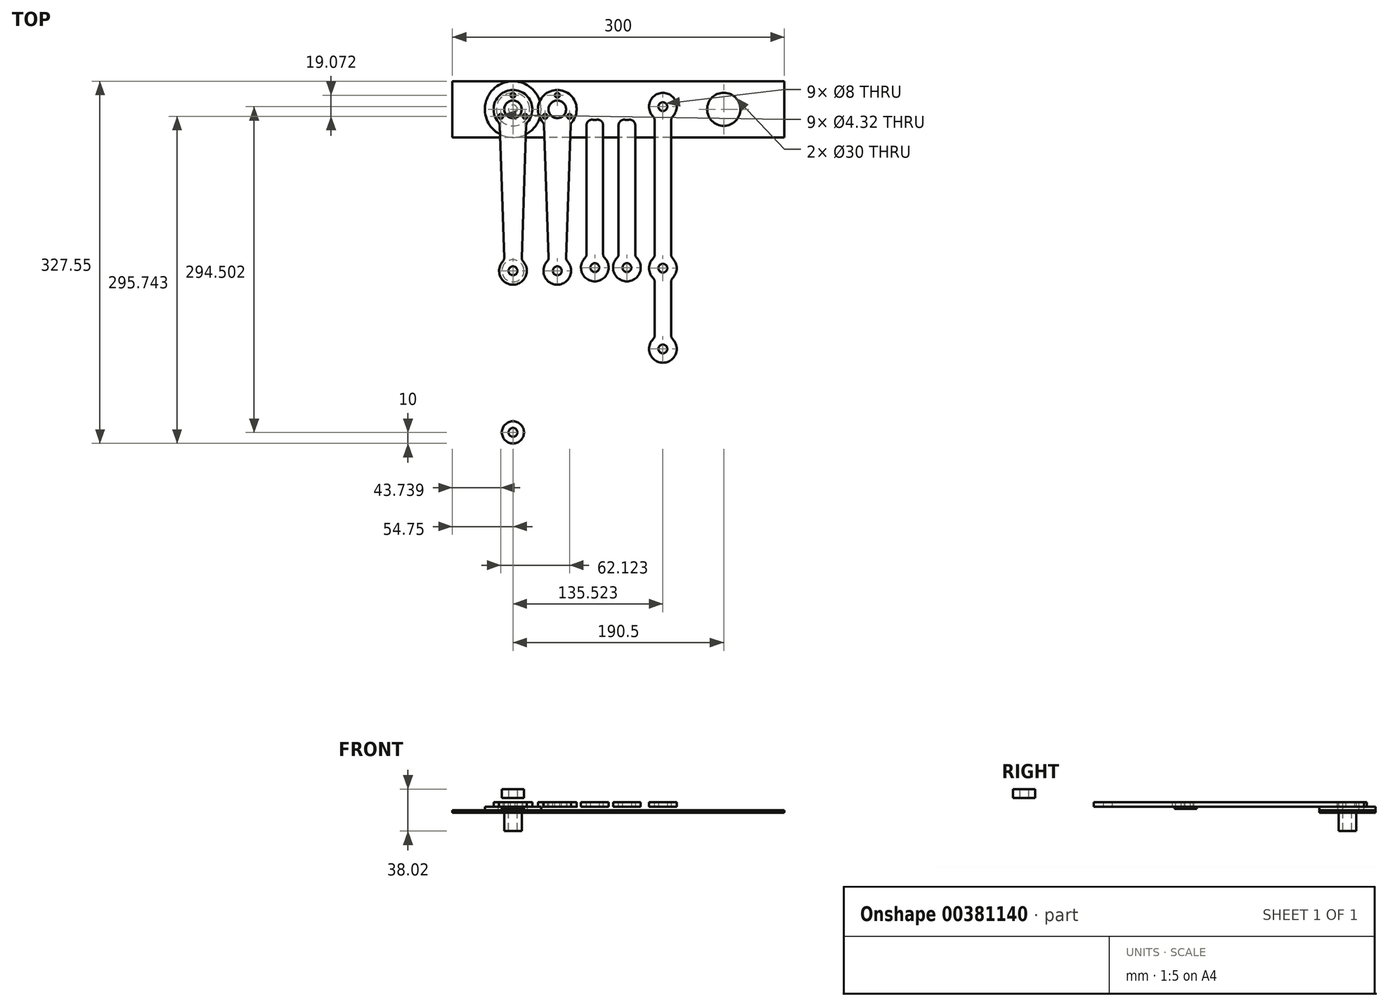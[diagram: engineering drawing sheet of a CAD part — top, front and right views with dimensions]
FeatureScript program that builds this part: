
annotation { "Feature Type Name" : "Feature", "Feature Type Description" : "" }
export const myFeature = defineFeature(function(context is Context, id is Id, definition is map)
    precondition{}
    {
        {
            var Q0;
            Q0=qCreatedBy(makeId("Top.planeOp"),FACE);
            var sketch = newSketch(context, id + "F0", { "sketchPlane" : qUnion([Q0])});
            skCircle(sketch, "E0", {"center": v(0, 0) * mm, "radius": 25.4 * mm});
            skCircle(sketch, "E1", {"center": v(0, 0) * mm, "radius": 7.93 * mm});
            skCircle(sketch, "E2", {"center": v(0, 0) * mm, "radius": 4 * mm});
            skSolve(sketch);
        }
        {
            var Q0;
            Q0=makeQuery(id+"F0.imprint","IMPRINT",FACE,{"disambiguationData":[TD([[makeQuery(id+"F0.imprint","IMPRINT",EDGE,{"derivedFrom":sQuery(id+"F0.wireOp",EDGE,"E0")}),1.0]])]});
            var Q1;
            Q1=makeQuery(id+"F0.imprint","IMPRINT",FACE,{"disambiguationData":[TD([[makeQuery(id+"F0.imprint","IMPRINT",EDGE,{"derivedFrom":sQuery(id+"F0.wireOp",EDGE,"E1")}),1.0]])]});
            var Q2;
            Q2=makeQuery(id+"F0.imprint","IMPRINT",FACE,{"disambiguationData":[TD([[makeQuery(id+"F0.imprint","IMPRINT",EDGE,{"derivedFrom":sQuery(id+"F0.wireOp",EDGE,"E2")}),1.0]])]});
            var Q3;
            Q3=sQuery(id+"F0.wireOp",EDGE,"E0");
            var Q4;
            Q4=sQuery(id+"F0.wireOp",EDGE,"E1");
            var Q5;
            Q5=sQuery(id+"F0.wireOp",EDGE,"E2");
            extrude(context, id + "F1", {"entities" : qUnion([Q0, Q1, Q2]), "surfaceEntities" : qUnion([Q3, Q4, Q5]), "depth" : 3.17 * mm});
        }
        {
            var Q0;
            Q0=makeQuery(id+"F0.imprint","IMPRINT",FACE,{"disambiguationData":[TD([[makeQuery(id+"F0.imprint","IMPRINT",EDGE,{"derivedFrom":sQuery(id+"F0.wireOp",EDGE,"E1")}),1.0]])]});
            extrude(context, id + "F2", {"entities" : qUnion([Q0]), "operationType" : NewBodyOperationType.ADD, "oppositeDirection" : true, "depth" : 18.85 * mm});
        }
        {
            var Q0;
            Q0=makeQuery(id+"F1.opExtrude","CAP_FACE",FACE,{"disambiguationData":[OSD([sQuery(id+"F0.wireOp",EDGE,"E0")])],"isStart":false});
            var sketch = newSketch(context, id + "F3", { "sketchPlane" : qUnion([Q0])});
            skLineSegment(sketch, "E3", {"start": v(-17.51, 0) * mm, "end": v(-12.5, -146.05) * mm});
            skLineSegment(sketch, "E4", {"start": v(17.51, 0) * mm, "end": v(12.5, -146.05) * mm});
            skCircle(sketch, "E5", {"center": v(0, 0) * mm, "radius": 17.5 * mm});
            skCircle(sketch, "E6", {"center": v(0, -146.05) * mm, "radius": 12.5 * mm});
            skLineSegment(sketch, "E7", {"start": v(-12.07, -12.67) * mm, "end": v(-7.83, -136.3) * mm});
            skLineSegment(sketch, "E8", {"start": v(12.07, -12.67) * mm, "end": v(7.84, -136.31) * mm});
            skCircle(sketch, "E9.0", {"center": v(0, 0) * mm, "radius": 7.93 * mm});
            skSolve(sketch);
        }
        {
            var Q0;
            {var subQ0=sQuery(id+"F3.wireOp",EDGE,"E5");var subQ1=makeQuery(id+"F3.imprint","INTERSECT",VERTEX,{"derivedFrom":[sQuery(id+"F3.wireOp",EDGE,"E3"),subQ0]});Q0=makeQuery(id+"F3.imprint","IMPRINT",FACE,{"disambiguationData":[TD([[makeQuery(id+"F3.imprint","IMPRINT",EDGE,{"disambiguationData":[TD([[subQ1,1.0]])],"derivedFrom":subQ0}),1.0]])]});}
            var Q1;
            {var subQ0=sQuery(id+"F3.wireOp",EDGE,"E7");var subQ1=sQuery(id+"F3.wireOp",EDGE,"E5");var subQ2=makeQuery(id+"F3.imprint","INTERSECT",VERTEX,{"derivedFrom":[subQ1,subQ0]});Q1=makeQuery(id+"F3.imprint","IMPRINT",FACE,{"disambiguationData":[TD([[makeQuery(id+"F3.imprint","IMPRINT",EDGE,{"disambiguationData":[TD([[subQ2,-1.0]])],"derivedFrom":subQ1}),-1.0]])]});}
            var Q2;
            {var subQ0=sQuery(id+"F3.wireOp",EDGE,"E6");var subQ1=makeQuery(id+"F3.imprint","INTERSECT",VERTEX,{"derivedFrom":[sQuery(id+"F3.wireOp",EDGE,"E4"),subQ0]});Q2=makeQuery(id+"F3.imprint","IMPRINT",FACE,{"disambiguationData":[TD([[makeQuery(id+"F3.imprint","IMPRINT",EDGE,{"disambiguationData":[TD([[subQ1,-1.0]])],"derivedFrom":subQ0}),1.0]])]});}
            var Q3;
            {var subQ0=sQuery(id+"F3.wireOp",EDGE,"E7");var subQ1=sQuery(id+"F3.wireOp",EDGE,"E6");var subQ2=makeQuery(id+"F3.imprint","INTERSECT",VERTEX,{"derivedFrom":[subQ1,subQ0]});Q3=makeQuery(id+"F3.imprint","IMPRINT",FACE,{"disambiguationData":[TD([[makeQuery(id+"F3.imprint","IMPRINT",EDGE,{"disambiguationData":[TD([[subQ2,1.0]])],"derivedFrom":subQ1}),-1.0]])]});}
            extrude(context, id + "F4", {"entities" : qUnion([Q0, Q1, Q2, Q3]), "depth" : 4 * mm});
        }
        {
            var Q0;
            Q0=makeQuery(id+"F4.opExtrude","SWEPT_EDGE",EDGE,{"disambiguationData":[OSD([sQuery(id+"F3.wireOp",EDGE,"E5"),sQuery(id+"F3.wireOp",EDGE,"E7")])]});
            var Q1;
            Q1=makeQuery(id+"F4.opExtrude","SWEPT_EDGE",EDGE,{"disambiguationData":[OSD([sQuery(id+"F3.wireOp",EDGE,"E5"),sQuery(id+"F3.wireOp",EDGE,"E8")])]});
            var Q2;
            Q2=makeQuery(id+"F4.opExtrude","SWEPT_EDGE",EDGE,{"disambiguationData":[OSD([sQuery(id+"F3.wireOp",EDGE,"E6"),sQuery(id+"F3.wireOp",EDGE,"E7")])]});
            var Q3;
            Q3=makeQuery(id+"F4.opExtrude","SWEPT_EDGE",EDGE,{"disambiguationData":[OSD([sQuery(id+"F3.wireOp",EDGE,"E6"),sQuery(id+"F3.wireOp",EDGE,"E8")])]});
            fillet(context, id + "F5", {"entities" : qUnion([Q0, Q1, Q2, Q3]), "radius" : 5 * mm, "tangentPropagation" : true, "allowEdgeOverflow" : false});
        }
        {
            var Q0;
            Q0=makeQuery(id+"F4.opExtrude","CAP_FACE",FACE,{"disambiguationData":[OSD([sQuery(id+"F3.wireOp",EDGE,"E5"),sQuery(id+"F3.wireOp",EDGE,"E6"),sQuery(id+"F3.wireOp",EDGE,"E7"),sQuery(id+"F3.wireOp",EDGE,"E8")])],"isStart":false});
            var sketch = newSketch(context, id + "F6", { "sketchPlane" : qUnion([Q0])});
            skPoint(sketch, "E10.center", {"position": v(0, 0) * mm});
            skCircle(sketch, "E11", {"center": v(0, -146.05) * mm, "radius": 4 * mm});
            skPoint(sketch, "E12", {"position": v(0, 12.71) * mm});
            skPoint(sketch, "E13.1.0", {"position": v(-11.01, -6.36) * mm});
            skPoint(sketch, "E13.2.0", {"position": v(11.01, -6.36) * mm});
            skSolve(sketch);
        }
        {
            var Q0;
            Q0=makeQuery(id+"F6.imprint","IMPRINT",FACE,{"disambiguationData":[TD([[makeQuery(id+"F6.imprint","IMPRINT",EDGE,{"derivedFrom":sQuery(id+"F6.wireOp",EDGE,"PpWmp2N7-R2N7-yGAy-fFJR-1MrLJnRTjxl5")}),1.0]])]});
            var Q1;
            Q1=makeQuery(id+"F6.imprint","IMPRINT",FACE,{"disambiguationData":[TD([[makeQuery(id+"F6.imprint","IMPRINT",EDGE,{"derivedFrom":sQuery(id+"F6.wireOp",EDGE,"E10.2.0")}),1.0]])]});
            var Q2;
            Q2=makeQuery(id+"F6.imprint","IMPRINT",FACE,{"disambiguationData":[TD([[makeQuery(id+"F6.imprint","IMPRINT",EDGE,{"derivedFrom":sQuery(id+"F6.wireOp",EDGE,"E10.1.0")}),1.0]])]});
            var Q3;
            Q3=makeQuery(id+"F6.imprint","IMPRINT",FACE,{"disambiguationData":[TD([[makeQuery(id+"F6.imprint","IMPRINT",EDGE,{"derivedFrom":sQuery(id+"F6.wireOp",EDGE,"E11")}),1.0]])]});
            extrude(context, id + "F7", {"entities" : qUnion([Q0, Q1, Q2, Q3]), "operationType" : NewBodyOperationType.REMOVE, "endBound" : BoundingType.THROUGH_ALL, "oppositeDirection" : true, "depth" : 25 * mm});
        }
        {
            var Q0;
            Q0=makeQuery(id+"F4.opExtrude","CAP_FACE",FACE,{"disambiguationData":[OSD([sQuery(id+"F3.wireOp",EDGE,"E5"),sQuery(id+"F3.wireOp",EDGE,"E6"),sQuery(id+"F3.wireOp",EDGE,"E7"),sQuery(id+"F3.wireOp",EDGE,"E8")])],"isStart":true});
            var sketch = newSketch(context, id + "F8", { "sketchPlane" : qUnion([Q0])});
            skCircle(sketch, "E14", {"center": v(0, 146.05) * mm, "radius": 10 * mm});
            skCircle(sketch, "E15.0", {"center": v(0, 146.05) * mm, "radius": 4 * mm});
            skSolve(sketch);
        }
        {
            var Q0;
            Q0=makeQuery(id+"F8.imprint","IMPRINT",FACE,{"disambiguationData":[TD([[makeQuery(id+"F8.imprint","IMPRINT",EDGE,{"derivedFrom":sQuery(id+"F8.wireOp",EDGE,"E14")}),1.0]])]});
            extrude(context, id + "F9", {"entities" : qUnion([Q0]), "depth" : 2 * mm});
        }
        {
            var Q0;
            {var subQ0=sQuery(id+"F0.wireOp",EDGE,"E0");Q0=makeQuery(id+"F2.boolean.opBoolean","SPLIT",FACE,{"disambiguationData":[TD([makeQuery(id+"F1.opExtrude","SWEPT_FACE",FACE,{"disambiguationData":[OSD([subQ0])]})])],"derivedFrom":makeQuery(id+"F1.opExtrude","CAP_FACE",FACE,{"disambiguationData":[OSD([subQ0])],"isStart":true})});}
            var sketch = newSketch(context, id + "F10", { "sketchPlane" : qUnion([Q0])});
            skCircle(sketch, "E16", {"center": v(0, 0) * mm, "radius": 15 * mm});
            skCircle(sketch, "E17", {"center": v(190.5, 0) * mm, "radius": 15 * mm});
            skLineSegment(sketch, "E18.bottom", {"start": v(245.25, -25.45) * mm, "end": v(-54.75, -25.45) * mm});
            skLineSegment(sketch, "E18.top", {"start": v(245.25, 25.45) * mm, "end": v(-54.75, 25.45) * mm});
            skLineSegment(sketch, "E18.left", {"start": v(245.25, -25.45) * mm, "end": v(245.25, 25.45) * mm});
            skLineSegment(sketch, "E18.right", {"start": v(-54.75, -25.45) * mm, "end": v(-54.75, 25.45) * mm});
            skLineSegment(sketch, "E19", {"start": v(245.25, 0) * mm, "end": v(-54.75, 0) * mm, "construction": true});
            skLineSegment(sketch, "E20", {"start": v(95.25, -25.45) * mm, "end": v(95.25, 25.45) * mm, "construction": true});
            skSolve(sketch);
        }
        {
            var Q0;
            Q0=makeQuery(id+"F10.imprint","IMPRINT",FACE,{"disambiguationData":[TD([[makeQuery(id+"F10.imprint","IMPRINT",EDGE,{"derivedFrom":sQuery(id+"F10.wireOp",EDGE,"E17")}),-1.0]])]});
            var Q1;
            Q1=makeQuery(id+"F10.imprint","IMPRINT",FACE,{"disambiguationData":[TD([[makeQuery(id+"F10.imprint","IMPRINT",EDGE,{"derivedFrom":sQuery(id+"F10.wireOp",EDGE,"E16")}),-1.0]])]});
            extrude(context, id + "F11", {"entities" : qUnion([Q0, Q1]), "depth" : 2.3 * mm});
        }
        {
            var Q0;
            Q0=makeQuery(id+"F4.opExtrude","CAP_FACE",FACE,{"disambiguationData":[OSD([sQuery(id+"F3.wireOp",EDGE,"E5"),sQuery(id+"F3.wireOp",EDGE,"E6"),sQuery(id+"F3.wireOp",EDGE,"E7"),sQuery(id+"F3.wireOp",EDGE,"E8")])],"isStart":false});
            var sketch = newSketch(context, id + "F12", { "sketchPlane" : qUnion([Q0])});
            skLineSegment(sketch, "E21", {"start": v(-12.5, -146.05) * mm, "end": v(-12.5, -292.1) * mm});
            skLineSegment(sketch, "E22", {"start": v(12.5, -146.05) * mm, "end": v(12.5, -292.1) * mm});
            skCircle(sketch, "E23", {"center": v(0, -146.05) * mm, "radius": 12.5 * mm});
            skCircle(sketch, "E24", {"center": v(0, -292.1) * mm, "radius": 12.5 * mm});
            skLineSegment(sketch, "E25", {"start": v(-7.5, -156.05) * mm, "end": v(-7.5, -282.1) * mm});
            skLineSegment(sketch, "E26", {"start": v(7.5, -156.05) * mm, "end": v(7.5, -282.1) * mm});
            skCircle(sketch, "E27", {"center": v(0, -292.1) * mm, "radius": 4 * mm});
            skSolve(sketch);
        }
        {
            var Q0;
            Q0=makeQuery(id+"F12.imprint","IMPRINT",FACE,{"disambiguationData":[TD([[makeQuery(id+"F12.imprint","IMPRINT",EDGE,{"derivedFrom":makeQuery(id+"F7.boolean.opBoolean","COPY",EDGE,{"derivedFrom":makeQuery(id+"F7.opExtrude","CAP_EDGE",EDGE,{"disambiguationData":[OSD([sQuery(id+"F6.wireOp",EDGE,"E11")])],"isStart":true})})}),-1.0]])]});
            var Q1;
            {var subQ0=sQuery(id+"F12.wireOp",EDGE,"E25");Q1=makeQuery(id+"F12.imprint","IMPRINT",FACE,{"disambiguationData":[TD([[makeQuery(id+"F12.imprint","IMPRINT",EDGE,{"derivedFrom":subQ0}),1.0]])]});}
            var Q2;
            Q2=makeQuery(id+"F12.imprint","IMPRINT",FACE,{"disambiguationData":[TD([[makeQuery(id+"F12.imprint","IMPRINT",EDGE,{"derivedFrom":sQuery(id+"F12.wireOp",EDGE,"E27")}),-1.0]])]});
            extrude(context, id + "F13", {"entities" : qUnion([Q0, Q1, Q2]), "depth" : 4 * mm});
        }
        {
            var Q0;
            Q0=makeQuery(id+"F13.opExtrude","SWEPT_EDGE",EDGE,{"disambiguationData":[OSD([sQuery(id+"F12.wireOp",EDGE,"E23"),sQuery(id+"F12.wireOp",EDGE,"E25")])]});
            var Q1;
            Q1=makeQuery(id+"F13.opExtrude","SWEPT_EDGE",EDGE,{"disambiguationData":[OSD([sQuery(id+"F12.wireOp",EDGE,"E24"),sQuery(id+"F12.wireOp",EDGE,"E25")])]});
            var Q2;
            Q2=makeQuery(id+"F13.opExtrude","SWEPT_EDGE",EDGE,{"disambiguationData":[OSD([sQuery(id+"F12.wireOp",EDGE,"E23"),sQuery(id+"F12.wireOp",EDGE,"E26")])]});
            var Q3;
            Q3=makeQuery(id+"F13.opExtrude","SWEPT_EDGE",EDGE,{"disambiguationData":[OSD([sQuery(id+"F12.wireOp",EDGE,"E24"),sQuery(id+"F12.wireOp",EDGE,"E26")])]});
            fillet(context, id + "F14", {"entities" : qUnion([Q0, Q1, Q2, Q3]), "radius" : 5 * mm, "tangentPropagation" : true, "allowEdgeOverflow" : false});
        }
        {
            var Q0;
            Q0=makeQuery(id+"F13.opExtrude","CAP_FACE",FACE,{"disambiguationData":[OSD([sQuery(id+"F6.wireOp",EDGE,"E11"),sQuery(id+"F12.wireOp",EDGE,"E23"),sQuery(id+"F12.wireOp",EDGE,"E24"),sQuery(id+"F12.wireOp",EDGE,"E25"),sQuery(id+"F12.wireOp",EDGE,"E26"),sQuery(id+"F12.wireOp",EDGE,"E27")])],"isStart":false});
            var sketch = newSketch(context, id + "F15", { "sketchPlane" : qUnion([Q0])});
            skCircle(sketch, "E28", {"center": v(0, -292.1) * mm, "radius": 10 * mm});
            skSolve(sketch);
        }
        {
            var Q0;
            Q0=makeQuery(id+"F15.imprint","IMPRINT",FACE,{"disambiguationData":[TD([[makeQuery(id+"F15.imprint","IMPRINT",EDGE,{"derivedFrom":sQuery(id+"F15.wireOp",EDGE,"E28")}),1.0]])]});
            extrude(context, id + "F16", {"entities" : qUnion([Q0]), "depth" : 8 * mm});
        }
        {
            var Q0;
            Q0=sQuery(id+"F6.wireOp",VERTEX,"E12");
            var Q1;
            Q1=sQuery(id+"F6.wireOp",VERTEX,"E13.2.0");
            var Q2;
            Q2=sQuery(id+"F6.wireOp",VERTEX,"E13.1.0");
            var Q3;
            Q3=makeQuery(id+"F1.opExtrude","SWEPT_BODY",BODY,{"disambiguationData":[OSD([sQuery(id+"F0.wireOp",EDGE,"E0")])]});
            var Q4;
            Q4=makeQuery(id+"F4.opExtrude","SWEPT_BODY",BODY,{"disambiguationData":[OSD([sQuery(id+"F3.wireOp",EDGE,"E5"),sQuery(id+"F3.wireOp",EDGE,"E6"),sQuery(id+"F3.wireOp",EDGE,"E7"),sQuery(id+"F3.wireOp",EDGE,"E8"),sQuery(id+"F3.wireOp",EDGE,"E9.0")])]});
            hole(context, id + "F17", {"style" : HoleStyle.SIMPLE, "endStyle" : HoleEndStyle.THROUGH, "standardTappedOrClearance" : lookupTablePath({ "standard" : "ANSI", "fit" : "Close", "size" : "#8", "type" : "Clearance" }), "standardBlindInLast" : lookupTablePath({ "fit" : "Close", "standard" : "ANSI", "size" : "#8", "type" : "Clearance" }), "holeDiameter" : 4.32 * mm, "isTappedThrough" : true, "tappedDepth" : 6.2 * mm, "tapClearance" : 3, "locations" : qUnion([Q0, Q1, Q2]), "scope" : qUnion([Q3, Q4])});
        }
        {
            var Q0;
            Q0=makeQuery(id+"F13.opExtrude","CAP_FACE",FACE,{"disambiguationData":[OSD([sQuery(id+"F6.wireOp",EDGE,"E11"),sQuery(id+"F12.wireOp",EDGE,"E23"),sQuery(id+"F12.wireOp",EDGE,"E24"),sQuery(id+"F12.wireOp",EDGE,"E25"),sQuery(id+"F12.wireOp",EDGE,"E26"),sQuery(id+"F12.wireOp",EDGE,"E27")])],"isStart":false});
            var sketch = newSketch(context, id + "F18", { "sketchPlane" : qUnion([Q0])});
            skLineSegment(sketch, "E29", {"start": v(44.92, -100.2) * mm, "end": v(44.92, -246.25) * mm});
            skLineSegment(sketch, "E30", {"start": v(69.92, -100.2) * mm, "end": v(69.92, -246.25) * mm});
            skCircle(sketch, "E31", {"center": v(57.42, -100.2) * mm, "radius": 12.5 * mm});
            skCircle(sketch, "E32", {"center": v(57.42, -246.25) * mm, "radius": 12.5 * mm});
            skLineSegment(sketch, "E33", {"start": v(49.92, -110.2) * mm, "end": v(49.92, -236.25) * mm});
            skLineSegment(sketch, "E34", {"start": v(64.92, -110.2) * mm, "end": v(64.92, -236.25) * mm});
            skCircle(sketch, "E35", {"center": v(57.42, -246.25) * mm, "radius": 4 * mm});
            skCircle(sketch, "E36", {"center": v(57.42, -319.27) * mm, "radius": 12.5 * mm});
            skLineSegment(sketch, "E37", {"start": v(49.92, -309.27) * mm, "end": v(49.92, -256.25) * mm});
            skLineSegment(sketch, "E38", {"start": v(64.92, -256.25) * mm, "end": v(64.92, -309.27) * mm});
            skCircle(sketch, "E39", {"center": v(57.42, -100.2) * mm, "radius": 4 * mm});
            skCircle(sketch, "E40", {"center": v(57.42, -319.27) * mm, "radius": 4 * mm});
            skSolve(sketch);
        }
        {
            var Q0;
            Q0=makeQuery(id+"F18.imprint","IMPRINT",FACE,{"disambiguationData":[TD([[makeQuery(id+"F18.imprint","IMPRINT",EDGE,{"derivedFrom":sQuery(id+"F18.wireOp",EDGE,"E39")}),-1.0]])]});
            var Q1;
            {var subQ0=sQuery(id+"F18.wireOp",EDGE,"E33");Q1=makeQuery(id+"F18.imprint","IMPRINT",FACE,{"disambiguationData":[TD([[makeQuery(id+"F18.imprint","IMPRINT",EDGE,{"derivedFrom":subQ0}),1.0]])]});}
            var Q2;
            Q2=makeQuery(id+"F18.imprint","IMPRINT",FACE,{"disambiguationData":[TD([[makeQuery(id+"F18.imprint","IMPRINT",EDGE,{"derivedFrom":sQuery(id+"F18.wireOp",EDGE,"E35")}),-1.0]])]});
            var Q3;
            {var subQ0=sQuery(id+"F18.wireOp",EDGE,"E37");Q3=makeQuery(id+"F18.imprint","IMPRINT",FACE,{"disambiguationData":[TD([[makeQuery(id+"F18.imprint","IMPRINT",EDGE,{"derivedFrom":subQ0}),-1.0]])]});}
            var Q4;
            Q4=makeQuery(id+"F18.imprint","IMPRINT",FACE,{"disambiguationData":[TD([[makeQuery(id+"F18.imprint","IMPRINT",EDGE,{"derivedFrom":sQuery(id+"F18.wireOp",EDGE,"E40")}),-1.0]])]});
            extrude(context, id + "F19", {"entities" : qUnion([Q0, Q1, Q2, Q3, Q4]), "depth" : 4 * mm});
        }
        {
            var Q0;
            Q0=makeQuery(id+"F19.opExtrude","SWEPT_EDGE",EDGE,{"disambiguationData":[OSD([sQuery(id+"F18.wireOp",EDGE,"E31"),sQuery(id+"F18.wireOp",EDGE,"E33")])]});
            var Q1;
            Q1=makeQuery(id+"F19.opExtrude","SWEPT_EDGE",EDGE,{"disambiguationData":[OSD([sQuery(id+"F18.wireOp",EDGE,"E31"),sQuery(id+"F18.wireOp",EDGE,"E34")])]});
            var Q2;
            Q2=makeQuery(id+"F19.opExtrude","SWEPT_EDGE",EDGE,{"disambiguationData":[OSD([sQuery(id+"F18.wireOp",EDGE,"E32"),sQuery(id+"F18.wireOp",EDGE,"E34")])]});
            var Q3;
            Q3=makeQuery(id+"F19.opExtrude","SWEPT_EDGE",EDGE,{"disambiguationData":[OSD([sQuery(id+"F18.wireOp",EDGE,"E32"),sQuery(id+"F18.wireOp",EDGE,"E38")])]});
            var Q4;
            Q4=makeQuery(id+"F19.opExtrude","SWEPT_EDGE",EDGE,{"disambiguationData":[OSD([sQuery(id+"F18.wireOp",EDGE,"E36"),sQuery(id+"F18.wireOp",EDGE,"E38")])]});
            var Q5;
            Q5=makeQuery(id+"F19.opExtrude","SWEPT_EDGE",EDGE,{"disambiguationData":[OSD([sQuery(id+"F18.wireOp",EDGE,"E36"),sQuery(id+"F18.wireOp",EDGE,"E37")])]});
            var Q6;
            Q6=makeQuery(id+"F19.opExtrude","SWEPT_EDGE",EDGE,{"disambiguationData":[OSD([sQuery(id+"F18.wireOp",EDGE,"E32"),sQuery(id+"F18.wireOp",EDGE,"E37")])]});
            var Q7;
            Q7=makeQuery(id+"F19.opExtrude","SWEPT_EDGE",EDGE,{"disambiguationData":[OSD([sQuery(id+"F18.wireOp",EDGE,"E32"),sQuery(id+"F18.wireOp",EDGE,"E33")])]});
            fillet(context, id + "F20", {"entities" : qUnion([Q0, Q1, Q2, Q3, Q4, Q5, Q6, Q7]), "radius" : 5 * mm, "tangentPropagation" : true, "allowEdgeOverflow" : false});
        }
        {
            var Q0;
            Q0=makeQuery(id+"F4.opExtrude","SWEPT_BODY",BODY,{"disambiguationData":[OSD([sQuery(id+"F3.wireOp",EDGE,"E5"),sQuery(id+"F3.wireOp",EDGE,"E6"),sQuery(id+"F3.wireOp",EDGE,"E7"),sQuery(id+"F3.wireOp",EDGE,"E8"),sQuery(id+"F3.wireOp",EDGE,"E9.0")])]});
            transform(context, id + "F21", {"entities" : qUnion([Q0]), "transformType" : TransformType.TRANSLATION_3D, "dx" : 40.1 * mm, "dy" : 0 * mm, "dz" : 0 * mm, "makeCopy" : true});
        }
        {
            var Q0;
            Q0=makeQuery(id+"F13.opExtrude","SWEPT_BODY",BODY,{"disambiguationData":[OSD([sQuery(id+"F6.wireOp",EDGE,"E11"),sQuery(id+"F12.wireOp",EDGE,"E23"),sQuery(id+"F12.wireOp",EDGE,"E24"),sQuery(id+"F12.wireOp",EDGE,"E25"),sQuery(id+"F12.wireOp",EDGE,"E26"),sQuery(id+"F12.wireOp",EDGE,"E27")])]});
            transform(context, id + "F22", {"entities" : qUnion([Q0]), "transformType" : TransformType.TRANSLATION_3D, "dx" : 74 * mm, "dy" : 149 * mm, "dz" : -4 * mm, "makeCopy" : false});
        }
        {
            var Q0;
            Q0=makeQuery(id+"F19.opExtrude","SWEPT_BODY",BODY,{"disambiguationData":[OSD([sQuery(id+"F18.wireOp",EDGE,"E31"),sQuery(id+"F18.wireOp",EDGE,"E32"),sQuery(id+"F18.wireOp",EDGE,"E33"),sQuery(id+"F18.wireOp",EDGE,"E34"),sQuery(id+"F18.wireOp",EDGE,"E35"),sQuery(id+"F18.wireOp",EDGE,"E36"),sQuery(id+"F18.wireOp",EDGE,"E37"),sQuery(id+"F18.wireOp",EDGE,"E38"),sQuery(id+"F18.wireOp",EDGE,"E39"),sQuery(id+"F18.wireOp",EDGE,"E40")])]});
            transform(context, id + "F23", {"entities" : qUnion([Q0]), "transformType" : TransformType.TRANSLATION_3D, "dx" : 78.1 * mm, "dy" : 102.6 * mm, "dz" : -8 * mm, "makeCopy" : false});
        }
        {
            var Q0;
            Q0=makeQuery(id+"F13.opExtrude","SWEPT_BODY",BODY,{"disambiguationData":[OSD([sQuery(id+"F6.wireOp",EDGE,"E11"),sQuery(id+"F12.wireOp",EDGE,"E23"),sQuery(id+"F12.wireOp",EDGE,"E24"),sQuery(id+"F12.wireOp",EDGE,"E25"),sQuery(id+"F12.wireOp",EDGE,"E26"),sQuery(id+"F12.wireOp",EDGE,"E27")])]});
            transform(context, id + "F24", {"entities" : qUnion([Q0]), "transformType" : TransformType.TRANSLATION_3D, "dx" : 29 * mm, "dy" : 0 * mm, "dz" : 0 * mm, "makeCopy" : true});
        }
    });
